# Revit family: Window_Swing_Flush_Ready-Access_FM3X
name_source: partatom
category: Windows
units: mm (PartAtom-declared; Revit-internal decimal feet)

## family parameters
Always vertical = Yes
Classification Number = 23.30.20.24.14
Cut with Voids When Loaded = No
Host = Wall
Room Calculation Point = No
Shared = No

## types (1)
- 18x18 Manual Outward Swing
    Air Infiltration = as Specified
    Assembly Code = B2020100
    Construction Details = http://www.arcat.com
    Description = Ready Access Manual Outward Swinging Service Window - FM3X as Specified
    Expected Lifespan (Years) = 0
    Forced Entry Rating = as Specified
    Frame Thickness = 1' - 2 1/4"
    Height = 2' - 2"
    Keynote = 08582
    Maintenance Schedule (Months) = 0
    Manufacturer = Ready Access
    Manufacturer Fax = 630-876-7767
    Manufacturer Website = http://www.ready-access.com
    Meets Egress = as Specified
    Miami Dade Conformance = as Specified
    Model = FM3X
    Product Data = http://www.arcat.com
    Sales Information = http://www.ready-access.com
    Send Message = http://www.arcat.com
    Service Opening Height = 1' - 6"
    Service Opening Width = 1' - 6"
    Sound Transmission Class (STC) = 0
    Specification = http://www.arcat.com
    Standards Conformance = as Specified
    Structural Test Pressure = as Specified
    URL = http://www.ready-access.com
    Wall Closure = By host
    Warranty Duration (Years) = 0
    Water Penetration = as Specified
    Width = 2' - 3 1/4"

## geometry (parser evidence)
native form markers: Sweep x3
no freeform markers — native parametric forms only
